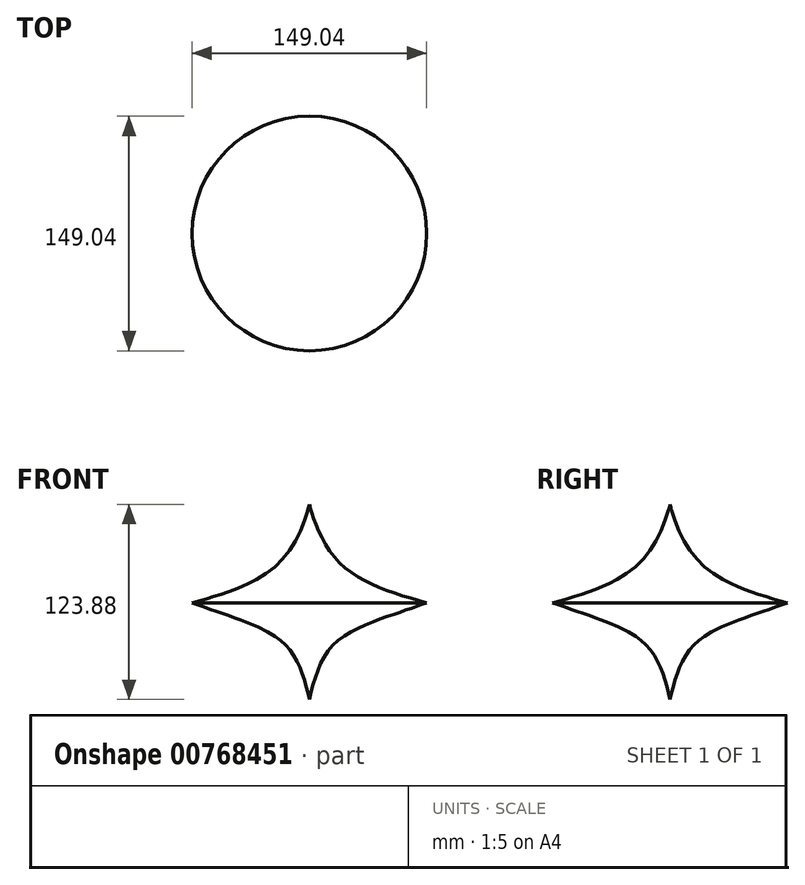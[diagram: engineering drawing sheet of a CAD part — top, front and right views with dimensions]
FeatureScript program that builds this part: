
annotation { "Feature Type Name" : "Feature", "Feature Type Description" : "" }
export const myFeature = defineFeature(function(context is Context, id is Id, definition is map)
    precondition{}
    {
        {
            var Q0;
            Q0=qCreatedBy(makeId("Front.planeOp"),FACE);
            var sketch = newSketch(context, id + "F0", { "sketchPlane" : qUnion([Q0])});
            skLineSegment(sketch, "E0", {"start": v(0, 74.79) * mm, "end": v(0, -75.33) * mm});
            skFitSpline(sketch, "E1", {"points": [v(0, 62.89) * mm, v(0, 62.62) * mm, v(15.01, 30.16) * mm, v(74.52, 0) * mm], "startDerivative": vector(-0.98, -4.2) * mm, "endDerivative": vector(123.84, -35.43) * mm});
            skFitSpline(sketch, "E2", {"points": [v(74.52, 0) * mm, v(51.53, -7.98) * mm, v(15.01, -26.91) * mm, v(0, -61.26) * mm], "startDerivative": vector(-73.78, -25.58) * mm, "endDerivative": vector(-26.58, -108.5) * mm});
            skSolve(sketch);
        }
        {
            var Q0;
            {var subQ0=sQuery(id+"F0.wireOp",EDGE,"E2");Q0=makeQuery(id+"F0.imprint","IMPRINT",FACE,{"disambiguationData":[TD([[makeQuery(id+"F0.imprint","IMPRINT",EDGE,{"derivedFrom":subQ0}),-1.0]])]});}
            var Q1;
            Q1=sQuery(id+"F0.wireOp",EDGE,"E0");
            revolve(context, id + "F1", {"surfaceOperationType" : NewSurfaceOperationType.NEW, "entities" : qUnion([Q0]), "axis" : qUnion([Q1]), "revolveType" : RevolveType.FULL});
        }
    });
